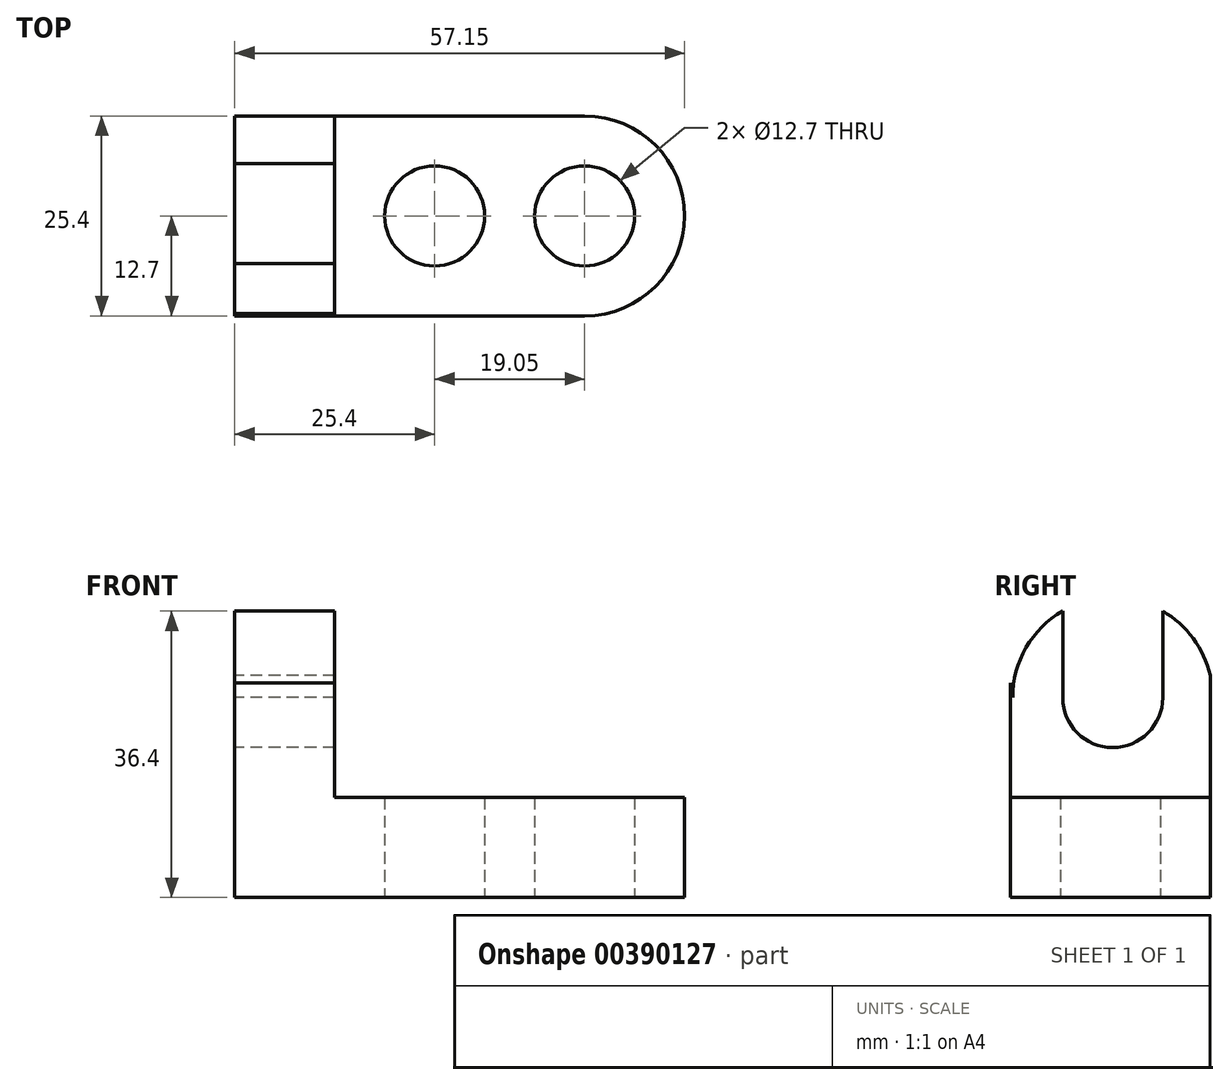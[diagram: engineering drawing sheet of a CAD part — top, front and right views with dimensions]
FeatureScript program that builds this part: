
annotation { "Feature Type Name" : "Feature", "Feature Type Description" : "" }
export const myFeature = defineFeature(function(context is Context, id is Id, definition is map)
    precondition{}
    {
        {
            var Q0;
            Q0=qCreatedBy(makeId("Front.planeOp"),FACE);
            var sketch = newSketch(context, id + "F0", { "sketchPlane" : qUnion([Q0])});
            skLineSegment(sketch, "E0", {"start": v(0, 0) * mm, "end": v(57.15, 0) * mm});
            skLineSegment(sketch, "E1", {"start": v(57.15, 0) * mm, "end": v(57.15, 12.7) * mm});
            skLineSegment(sketch, "E2", {"start": v(57.15, 12.7) * mm, "end": v(12.7, 12.7) * mm});
            skLineSegment(sketch, "E3", {"start": v(12.7, 12.7) * mm, "end": v(12.7, 38.1) * mm});
            skLineSegment(sketch, "E4", {"start": v(12.7, 38.1) * mm, "end": v(0, 38.1) * mm});
            skLineSegment(sketch, "E5", {"start": v(0, 38.1) * mm, "end": v(0, 0) * mm});
            skSolve(sketch);
        }
        {
            var Q0;
            Q0=makeQuery(id+"F0.imprint","IMPRINT",FACE,{"disambiguationData":[TD([[makeQuery(id+"F0.imprint","IMPRINT",EDGE,{"derivedFrom":sQuery(id+"F0.wireOp",EDGE,"E0")}),1.0]])]});
            extrude(context, id + "F1", {"entities" : qUnion([Q0]), "depth" : 25.4 * mm});
        }
        {
            var Q0;
            Q0=qCreatedBy(makeId("Top.planeOp"),FACE);
            var sketch = newSketch(context, id + "F2", { "sketchPlane" : qUnion([Q0])});
            skCircle(sketch, "E6", {"center": v(25.4, -12.7) * mm, "radius": 6.35 * mm});
            skCircle(sketch, "E7", {"center": v(44.45, -12.7) * mm, "radius": 6.35 * mm});
            skArc(sketch, "E8", {"start": v(44.45, 0) * mm, "mid": v(57.15, -12.7) * mm, "end": v(44.45, -25.4) * mm});
            skLineSegment(sketch, "E9", {"start": v(44.45, 0) * mm, "end": v(57.15, 0) * mm});
            skPoint(sketch, "E9.endSnap0", {"position": v(57.15, -12.7) * mm});
            skLineSegment(sketch, "E10", {"start": v(57.15, 0) * mm, "end": v(57.15, -25.4) * mm});
            skLineSegment(sketch, "E11", {"start": v(57.15, -25.4) * mm, "end": v(44.45, -25.4) * mm});
            skLineSegment(sketch, "E12", {"start": v(25.4, -6.35) * mm, "end": v(44.45, -6.35) * mm});
            skLineSegment(sketch, "E13", {"start": v(44.45, -6.35) * mm, "end": v(44.45, -19.05) * mm});
            skLineSegment(sketch, "E14", {"start": v(44.45, -19.05) * mm, "end": v(25.4, -19.05) * mm});
            skLineSegment(sketch, "E15", {"start": v(25.4, -19.05) * mm, "end": v(25.4, -6.35) * mm});
            skSolve(sketch);
        }
        {
            var Q0;
            {var subQ0=sQuery(id+"F2.wireOp",EDGE,"E15");Q0=makeQuery(id+"F2.imprint","IMPRINT",FACE,{"disambiguationData":[TD([[makeQuery(id+"F2.imprint","IMPRINT",EDGE,{"derivedFrom":subQ0}),1.0]])]});}
            var Q1;
            {var subQ0=sQuery(id+"F2.wireOp",EDGE,"E15");Q1=makeQuery(id+"F2.imprint","IMPRINT",FACE,{"disambiguationData":[TD([[makeQuery(id+"F2.imprint","IMPRINT",EDGE,{"derivedFrom":subQ0}),-1.0]])]});}
            var Q2;
            {var subQ0=sQuery(id+"F2.wireOp",EDGE,"E13");Q2=makeQuery(id+"F2.imprint","IMPRINT",FACE,{"disambiguationData":[TD([[makeQuery(id+"F2.imprint","IMPRINT",EDGE,{"derivedFrom":subQ0}),-1.0]])]});}
            var Q3;
            {var subQ0=sQuery(id+"F2.wireOp",EDGE,"E13");Q3=makeQuery(id+"F2.imprint","IMPRINT",FACE,{"disambiguationData":[TD([[makeQuery(id+"F2.imprint","IMPRINT",EDGE,{"derivedFrom":subQ0}),1.0]])]});}
            var Q4;
            {var subQ0=sQuery(id+"F2.wireOp",EDGE,"E11");Q4=makeQuery(id+"F2.imprint","IMPRINT",FACE,{"disambiguationData":[TD([[makeQuery(id+"F2.imprint","IMPRINT",EDGE,{"derivedFrom":subQ0}),-1.0]])]});}
            var Q5;
            {var subQ0=sQuery(id+"F2.wireOp",EDGE,"E9");Q5=makeQuery(id+"F2.imprint","IMPRINT",FACE,{"disambiguationData":[TD([[makeQuery(id+"F2.imprint","IMPRINT",EDGE,{"derivedFrom":subQ0}),-1.0]])]});}
            extrude(context, id + "F3", {"entities" : qUnion([Q0, Q1, Q2, Q3, Q4, Q5]), "operationType" : NewBodyOperationType.REMOVE, "depth" : 25.4 * mm});
        }
        {
            var Q0;
            Q0=qCreatedBy(makeId("Right.planeOp"),FACE);
            var sketch = newSketch(context, id + "F4", { "sketchPlane" : qUnion([Q0])});
            skCircle(sketch, "E16", {"center": v(-12.38, 25.4) * mm, "radius": 6.35 * mm});
            skLineSegment(sketch, "E17", {"start": v(-6.03, 25.4) * mm, "end": v(-6.03, 38.1) * mm});
            skLineSegment(sketch, "E18", {"start": v(-6.03, 38.1) * mm, "end": v(-18.73, 38.1) * mm});
            skLineSegment(sketch, "E19", {"start": v(-18.73, 38.1) * mm, "end": v(-18.73, 25.4) * mm});
            skArc(sketch, "E20", {"start": v(-25.08, 25.4) * mm, "mid": v(-12.38, 38.1) * mm, "end": v(0.32, 25.4) * mm});
            skLineSegment(sketch, "E21", {"start": v(0.32, 25.4) * mm, "end": v(0.32, 40.43) * mm});
            skLineSegment(sketch, "E22", {"start": v(0.32, 40.43) * mm, "end": v(-27.62, 40.43) * mm});
            skLineSegment(sketch, "E23", {"start": v(-27.62, 40.43) * mm, "end": v(-25.08, 25.4) * mm});
            skSolve(sketch);
        }
        {
            var Q0;
            {var subQ0=sQuery(id+"F4.wireOp",EDGE,"E16");var subQ1=makeQuery(id+"F4.imprint","INTERSECT",VERTEX,{"derivedFrom":[subQ0,sQuery(id+"F4.wireOp",EDGE,"E17")]});Q0=makeQuery(id+"F4.imprint","IMPRINT",FACE,{"disambiguationData":[TD([[makeQuery(id+"F4.imprint","IMPRINT",EDGE,{"disambiguationData":[TD([[subQ1,-1.0]])],"derivedFrom":subQ0}),1.0]])]});}
            var Q1;
            {var subQ4=sQuery(id+"F4.wireOp",EDGE,"E17");var subQ5=sQuery(id+"F4.wireOp",EDGE,"E16");var subQ6=makeQuery(id+"F4.imprint","INTERSECT",VERTEX,{"derivedFrom":[subQ5,subQ4]});Q1=makeQuery(id+"F4.imprint","IMPRINT",FACE,{"disambiguationData":[TD([[makeQuery(id+"F4.imprint","IMPRINT",EDGE,{"disambiguationData":[TD([[subQ6,-1.0]])],"derivedFrom":subQ5}),-1.0]])]});}
            var Q2;
            {var subQ5=sQuery(id+"F4.wireOp",EDGE,"E23");Q2=makeQuery(id+"F4.imprint","IMPRINT",FACE,{"disambiguationData":[TD([[makeQuery(id+"F4.imprint","IMPRINT",EDGE,{"derivedFrom":subQ5}),1.0]])]});}
            var Q3;
            {var subQ0=sQuery(id+"F4.wireOp",EDGE,"E22");var subQ1=sQuery(id+"F4.wireOp",EDGE,"E19");var subQ2=makeQuery(id+"F4.imprint","INTERSECT",VERTEX,{"derivedFrom":[subQ1,subQ0]});Q3=makeQuery(id+"F4.imprint","IMPRINT",FACE,{"disambiguationData":[TD([[makeQuery(id+"F4.imprint","IMPRINT",EDGE,{"disambiguationData":[TD([[subQ2,-1.0]])],"derivedFrom":subQ1}),1.0]])]});}
            var Q4;
            {var subQ0=sQuery(id+"F4.wireOp",EDGE,"E22");var subQ1=sQuery(id+"F4.wireOp",EDGE,"E17");var subQ2=makeQuery(id+"F4.imprint","INTERSECT",VERTEX,{"derivedFrom":[subQ1,subQ0]});Q4=makeQuery(id+"F4.imprint","IMPRINT",FACE,{"disambiguationData":[TD([[makeQuery(id+"F4.imprint","IMPRINT",EDGE,{"disambiguationData":[TD([[subQ2,1.0]])],"derivedFrom":subQ1}),1.0]])]});}
            var Q5;
            {var subQ5=sQuery(id+"F4.wireOp",EDGE,"E21");Q5=makeQuery(id+"F4.imprint","IMPRINT",FACE,{"disambiguationData":[TD([[makeQuery(id+"F4.imprint","IMPRINT",EDGE,{"derivedFrom":subQ5}),1.0]])]});}
            extrude(context, id + "F5", {"entities" : qUnion([Q0, Q1, Q2, Q3, Q4, Q5]), "operationType" : NewBodyOperationType.REMOVE, "depth" : 25.4 * mm});
        }
    });
